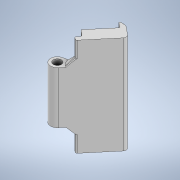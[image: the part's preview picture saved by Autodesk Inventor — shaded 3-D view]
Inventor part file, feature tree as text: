
AUTODESK INVENTOR PART (.ipt)
format: ipt  version: 2022 (Build 260153000, 153)  size: 282,624 bytes
history: native  units: mm
features: reference x16, fillet x8, other x5, extrude x4, sketch x4, projected_geometry x2, chamfer x1
ambient origin geometry x8: Origin, YZ Plane, XZ Plane, XY Plane, X Axis, Y Axis, Z Axis, Center Point
bodies: Body1 (feature_tree)
feature tree (40):
  other  "Твердое тело1"
  extrude  "Выдавливание1"  Depth=1.2mm
  extrude  "Выдавливание2"  Depth=2.0mm
  fillet  "Сопряжение1"  Radius=0.05mm
  fillet  "Сопряжение2"  Radius=7.7mm
  fillet  "Сопряжение3"  Radius=0.2mm
  fillet  "Сопряжение4"  Radius=0.3mm
  fillet  "Сопряжение5"  Radius=14.5mm
  extrude  "Выдавливание3"  Depth=0.15mm
  fillet  "Сопряжение6"  Radius=0.2mm
  fillet  "Сопряжение7"  Radius=0.5mm
  extrude  "Выдавливание4"  Depth=0.1mm
  fillet  "Сопряжение8"  Radius=1.0mm
  chamfer  "Фаска1"  Distance=0.1mm
  sketch  "Эскиз1"
  reference  "Ссылка1"
  reference  "Ссылка2"
  reference  "Ссылка3"
  reference  "Ссылка4"
  reference  "Ссылка5"
  reference  "Ссылка6"
  reference  "Ссылка7"
  reference  "Ссылка8"
  reference  "Ссылка9"
  reference  "Ссылка10"
  reference  "Ссылка11"
  reference  "Ссылка12"
  reference  "Ссылка13"
  sketch  "Эскиз2"
  projected_geometry  "Спроецированная петля1"
  reference  "Ссылка14"
  reference  "Ссылка15"
  sketch  "Эскиз3"
  reference  "Ссылка16"
  sketch  "Эскиз4"
  projected_geometry  "Спроецированная петля2"
  other  "<userpath>\Documents\Git\MZCAT_2024_construction\MZCAT_2024_RPI_2\MZCAT_4.iam"
  other  "MZCAT_4.iam"
  other  "motherboard_plate:1"
  other  "bottom_motherboard_skeleton:1"
